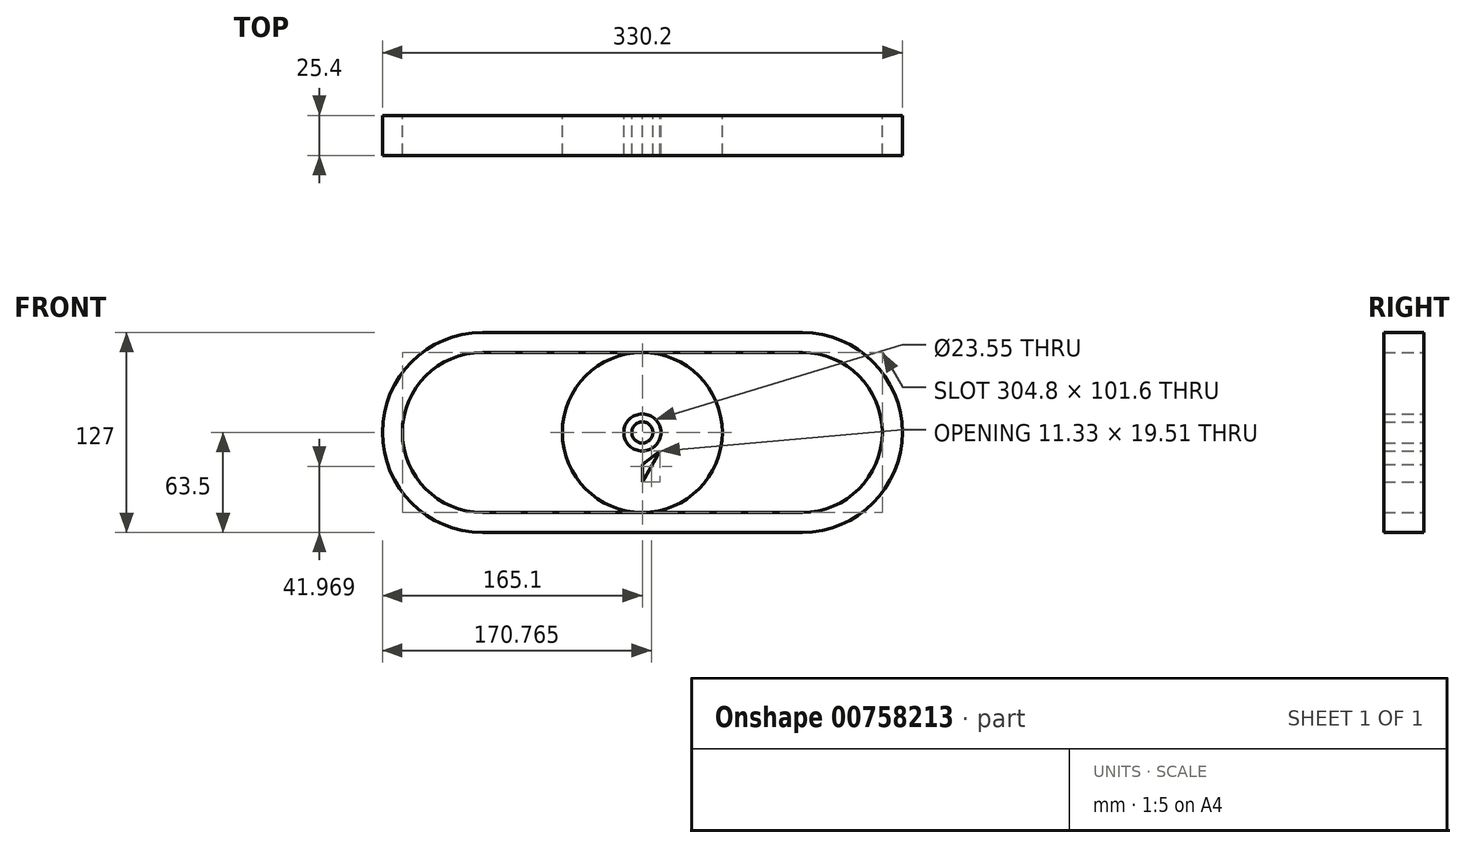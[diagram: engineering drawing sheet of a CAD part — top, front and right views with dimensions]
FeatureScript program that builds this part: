
annotation { "Feature Type Name" : "Feature", "Feature Type Description" : "" }
export const myFeature = defineFeature(function(context is Context, id is Id, definition is map)
    precondition{}
    {
        {
            var Q0;
            Q0=qCreatedBy(makeId("Front.planeOp"),FACE);
            var sketch = newSketch(context, id + "F0", { "sketchPlane" : qUnion([Q0])});
            skCircle(sketch, "E0", {"center": v(0, 0) * mm, "radius": 50.8 * mm});
            skLineSegment(sketch, "E1", {"start": v(0, 0) * mm, "end": v(101.6, 0) * mm});
            skLineSegment(sketch, "E2", {"start": v(0, 0) * mm, "end": v(-101.6, 0) * mm});
            skLineSegment(sketch, "E3", {"start": v(-101.6, 0) * mm, "end": v(-25.4, 44) * mm});
            skLineSegment(sketch, "E4", {"start": v(-101.6, 0) * mm, "end": v(-25.4, -44) * mm});
            skLineSegment(sketch, "E5", {"start": v(101.6, 0) * mm, "end": v(25.4, -44) * mm});
            skLineSegment(sketch, "E6", {"start": v(101.6, 0) * mm, "end": v(25.4, 44) * mm});
            skCircle(sketch, "E7", {"center": v(101.6, 0) * mm, "radius": 50.8 * mm});
            skCircle(sketch, "E8", {"center": v(-101.6, 0) * mm, "radius": 50.8 * mm});
            skArc(sketch, "E9", {"start": v(-101.6, 63.5) * mm, "mid": v(-165.1, 0) * mm, "end": v(-101.6, -63.5) * mm});
            skArc(sketch, "E10", {"start": v(101.6, -63.5) * mm, "mid": v(165.1, 0) * mm, "end": v(101.6, 63.5) * mm});
            skLineSegment(sketch, "E11", {"start": v(-101.6, 63.5) * mm, "end": v(101.6, 63.5) * mm});
            skLineSegment(sketch, "E12", {"start": v(101.6, -63.5) * mm, "end": v(-101.6, -63.5) * mm});
            skLineSegment(sketch, "E13", {"start": v(-101.6, 50.8) * mm, "end": v(101.6, 50.8) * mm});
            skLineSegment(sketch, "E14", {"start": v(101.6, -50.8) * mm, "end": v(-101.6, -50.8) * mm});
            skCircle(sketch, "E15", {"center": v(0, 0) * mm, "radius": 11.77 * mm});
            skLineSegment(sketch, "E16", {"start": v(0, -31.29) * mm, "end": v(0, -20.3) * mm});
            skLineSegment(sketch, "E17", {"start": v(11.33, -11.77) * mm, "end": v(0, -31.29) * mm});
            skLineSegment(sketch, "E18", {"start": v(11.33, -11.77) * mm, "end": v(0, -20.3) * mm});
            skPoint(sketch, "E19.orphan", {"position": v(0, -50.8) * mm});
            skCircle(sketch, "E20", {"center": v(0, 0) * mm, "radius": 6.7 * mm});
            skSolve(sketch);
        }
        {
            var Q0;
            {var subQ0=sQuery(id+"F0.wireOp",EDGE,"E0");var subQ5=makeQuery(id+"F0.imprint","INTERSECT",VERTEX,{"derivedFrom":[subQ0,sQuery(id+"F0.wireOp",EDGE,"E6")]});Q0=makeQuery(id+"F0.imprint","IMPRINT",FACE,{"disambiguationData":[TD([[makeQuery(id+"F0.imprint","IMPRINT",EDGE,{"disambiguationData":[TD([[subQ5,-1.0]])],"derivedFrom":subQ0}),1.0]])]});}
            var Q1;
            {var subQ0=sQuery(id+"F0.wireOp",EDGE,"E0");var subQ5=makeQuery(id+"F0.imprint","INTERSECT",VERTEX,{"derivedFrom":[subQ0,sQuery(id+"F0.wireOp",EDGE,"E4")]});Q1=makeQuery(id+"F0.imprint","IMPRINT",FACE,{"disambiguationData":[TD([[makeQuery(id+"F0.imprint","IMPRINT",EDGE,{"disambiguationData":[TD([[subQ5,-1.0]])],"derivedFrom":subQ0}),1.0]])]});}
            extrude(context, id + "F1", {"entities" : qUnion([Q0, Q1]), "depth" : 25.4 * mm, "offsetDistance" : 25.4 * mm});
        }
        {
            var Q0;
            Q0=makeQuery(id+"F0.imprint","IMPRINT",FACE,{"disambiguationData":[TD([[makeQuery(id+"F0.imprint","IMPRINT",EDGE,{"derivedFrom":sQuery(id+"F0.wireOp",EDGE,"E9")}),1.0]])]});
            extrude(context, id + "F2", {"entities" : qUnion([Q0]), "operationType" : NewBodyOperationType.ADD, "depth" : 25.4 * mm, "offsetDistance" : 25.4 * mm});
        }
        {
            var Q0;
            {var subQ0=sQuery(id+"F0.wireOp",EDGE,"E2");var subQ1=sQuery(id+"F0.wireOp",EDGE,"E1");var subQ2=makeQuery(id+"F0.imprint","INTERSECT",VERTEX,{"derivedFrom":[subQ1,subQ0]});Q0=makeQuery(id+"F0.imprint","IMPRINT",FACE,{"disambiguationData":[TD([[makeQuery(id+"F0.imprint","IMPRINT",EDGE,{"disambiguationData":[TD([[subQ2,-1.0]])],"derivedFrom":subQ1}),1.0]])]});}
            var Q1;
            {var subQ0=sQuery(id+"F0.wireOp",EDGE,"E2");var subQ1=sQuery(id+"F0.wireOp",EDGE,"E1");var subQ2=makeQuery(id+"F0.imprint","INTERSECT",VERTEX,{"derivedFrom":[subQ1,subQ0]});Q1=makeQuery(id+"F0.imprint","IMPRINT",FACE,{"disambiguationData":[TD([[makeQuery(id+"F0.imprint","IMPRINT",EDGE,{"disambiguationData":[TD([[subQ2,-1.0]])],"derivedFrom":subQ1}),-1.0]])]});}
            extrude(context, id + "F3", {"entities" : qUnion([Q0, Q1]), "depth" : 25.4 * mm, "offsetDistance" : 25.4 * mm});
        }
    });
